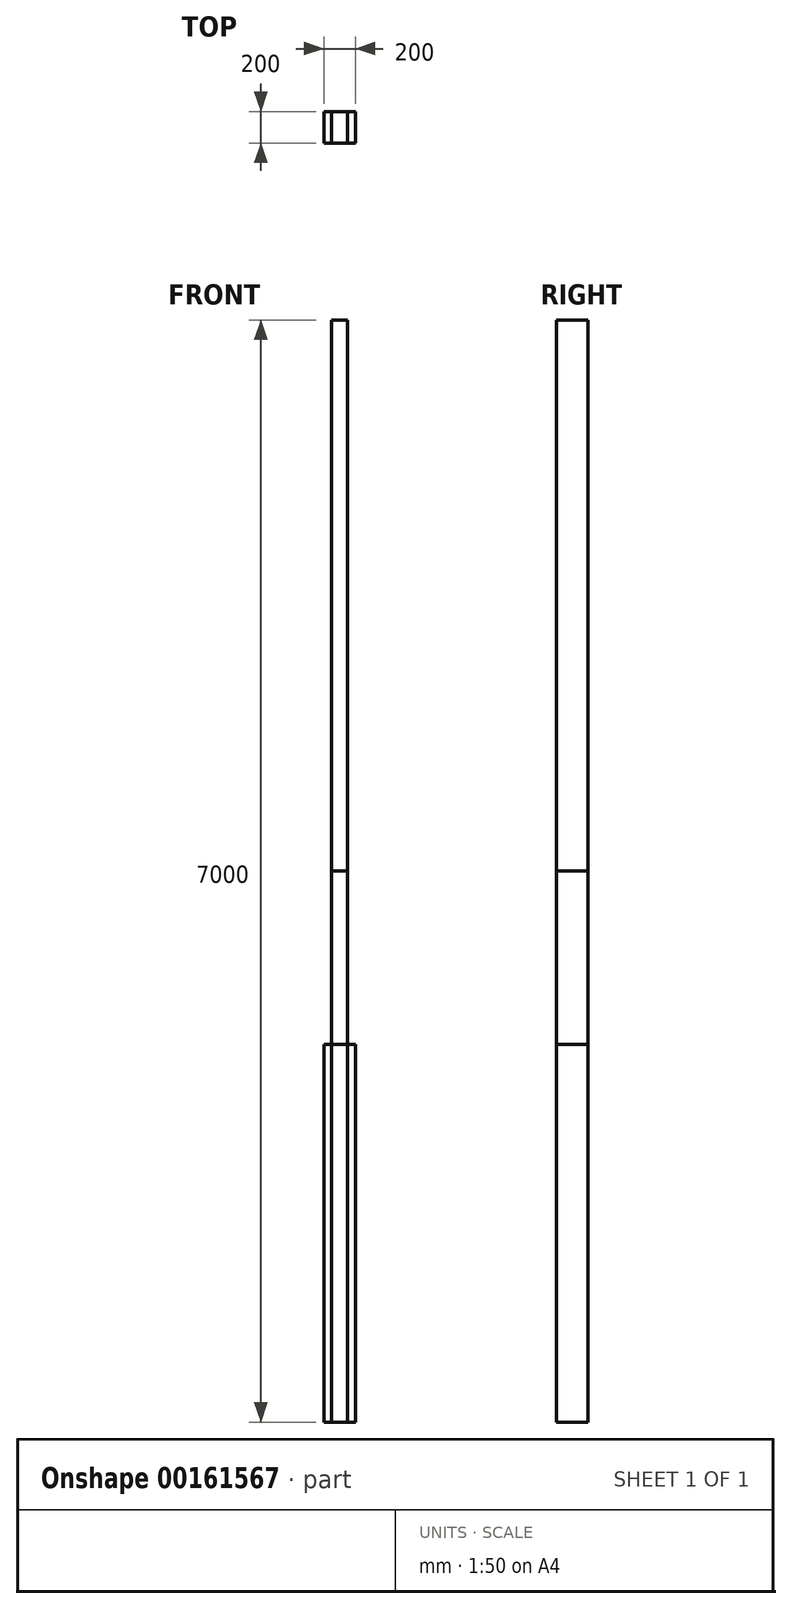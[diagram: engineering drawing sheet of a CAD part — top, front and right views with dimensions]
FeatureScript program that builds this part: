
annotation { "Feature Type Name" : "Feature", "Feature Type Description" : "" }
export const myFeature = defineFeature(function(context is Context, id is Id, definition is map)
    precondition{}
    {
        {
            var Q0;
            Q0=qCreatedBy(makeId("Top.planeOp"),FACE);
            var sketch = newSketch(context, id + "F0", { "sketchPlane" : qUnion([Q0])});
            skLineSegment(sketch, "E0.bottom", {"start": v(100, -100) * mm, "end": v(-100, -100) * mm});
            skLineSegment(sketch, "E0.top", {"start": v(100, 100) * mm, "end": v(-100, 100) * mm});
            skLineSegment(sketch, "E0.left", {"start": v(100, -100) * mm, "end": v(100, 100) * mm});
            skLineSegment(sketch, "E0.right", {"start": v(-100, -100) * mm, "end": v(-100, 100) * mm});
            skPoint(sketch, "E0.middle", {"position": v(0, 0) * mm});
            skSolve(sketch);
        }
        {
            var Q0;
            Q0=qCreatedBy(makeId("Top.planeOp"),FACE);
            var sketch = newSketch(context, id + "F1", { "sketchPlane" : qUnion([Q0])});
            skLineSegment(sketch, "E1.bottom", {"start": v(50, 100) * mm, "end": v(-50, 100) * mm});
            skLineSegment(sketch, "E1.top", {"start": v(50, -100) * mm, "end": v(-50, -100) * mm});
            skLineSegment(sketch, "E1.left", {"start": v(50, 100) * mm, "end": v(50, -100) * mm});
            skLineSegment(sketch, "E1.right", {"start": v(-50, 100) * mm, "end": v(-50, -100) * mm});
            skPoint(sketch, "E1.middle", {"position": v(0, 0) * mm});
            skSolve(sketch);
        }
        {
            var Q0;
            Q0 = qSketchRegion(id + "F0", true);
            extrude(context, id + "F2", {"entities" : qUnion([Q0]), "depth" : 2400 * mm});
        }
        {
            var Q0;
            Q0=makeQuery(id+"F1.imprint","IMPRINT",FACE,{"disambiguationData":[TD([[makeQuery(id+"F1.imprint","IMPRINT",EDGE,{"derivedFrom":sQuery(id+"F1.wireOp",EDGE,"E1.bottom")}),1.0]])]});
            extrude(context, id + "F3", {"entities" : qUnion([Q0]), "depth" : 3500 * mm});
        }
        {
            var Q0;
            Q0 = qSketchRegion(id + "F1", true);
            extrude(context, id + "F4", {"entities" : qUnion([Q0]), "depth" : 7000 * mm});
        }
    });
